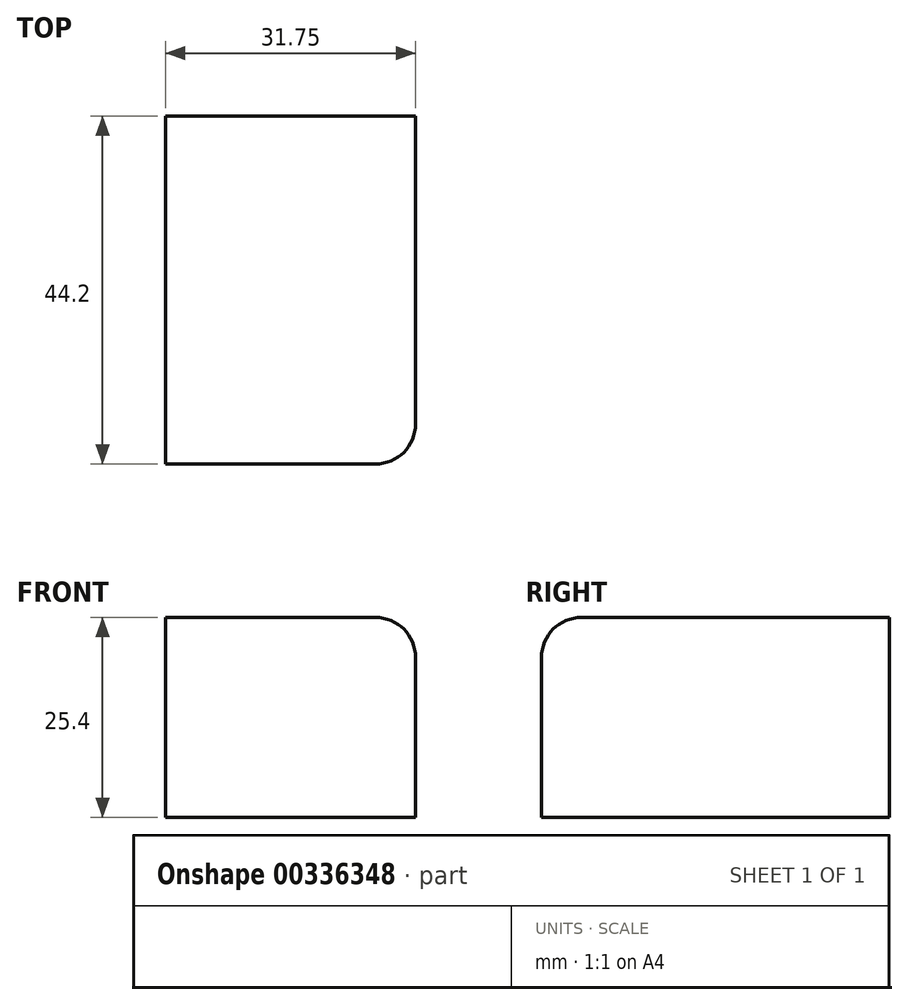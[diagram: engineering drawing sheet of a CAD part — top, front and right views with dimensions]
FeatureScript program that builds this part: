
annotation { "Feature Type Name" : "Feature", "Feature Type Description" : "" }
export const myFeature = defineFeature(function(context is Context, id is Id, definition is map)
    precondition{}
    {
        {
            var Q0;
            Q0=qCreatedBy(makeId("Front.planeOp"),FACE);
            var sketch = newSketch(context, id + "F0", { "sketchPlane" : qUnion([Q0])});
            skLineSegment(sketch, "E0.bottom", {"start": v(-12.7, 12.7) * mm, "end": v(19.05, 12.7) * mm});
            skLineSegment(sketch, "E0.top", {"start": v(-12.7, -12.7) * mm, "end": v(19.05, -12.7) * mm});
            skLineSegment(sketch, "E0.left", {"start": v(-12.7, 12.7) * mm, "end": v(-12.7, -12.7) * mm});
            skLineSegment(sketch, "E0.right", {"start": v(19.05, 12.7) * mm, "end": v(19.05, -12.7) * mm});
            skSolve(sketch);
        }
        {
            var Q0;
            Q0=makeQuery(id+"F0.imprint","IMPRINT",FACE,{"disambiguationData":[TD([[makeQuery(id+"F0.imprint","IMPRINT",EDGE,{"derivedFrom":sQuery(id+"F0.wireOp",EDGE,"E0.bottom")}),-1.0]])]});
            extrude(context, id + "F1", {"entities" : qUnion([Q0]), "depth" : 44.2 * mm});
        }
        {
            var Q0;
            Q0=makeQuery(id+"F1.opExtrude","CAP_EDGE",EDGE,{"disambiguationData":[OSD([sQuery(id+"F0.wireOp",EDGE,"E0.bottom")])],"isStart":false});
            var Q1;
            Q1=makeQuery(id+"F1.opExtrude","SWEPT_EDGE",EDGE,{"disambiguationData":[OSD([sQuery(id+"F0.wireOp",EDGE,"E0.bottom"),sQuery(id+"F0.wireOp",EDGE,"E0.right")])]});
            fillet(context, id + "F2", {"entities" : qUnion([Q0, Q1]), "radius" : 5.08 * mm, "tangentPropagation" : true, "allowEdgeOverflow" : false});
        }
        {
            var Q0;
            {var subQ0=sQuery(id+"F0.wireOp",EDGE,"E0.bottom");Q0=makeQuery(id+"F2.opFillet","BLEND_EDGE",EDGE,{"blendedFrom":[makeQuery(id+"F1.opExtrude","SWEPT_EDGE",EDGE,{"disambiguationData":[OSD([subQ0,sQuery(id+"F0.wireOp",EDGE,"E0.right")])]}),makeQuery(id+"F1.opExtrude","CAP_EDGE",EDGE,{"disambiguationData":[OSD([subQ0])],"isStart":false})],"blendedInto":[]});}
            fillet(context, id + "F3", {"entities" : qUnion([Q0]), "radius" : 5.08 * mm, "tangentPropagation" : true, "allowEdgeOverflow" : false});
        }
    });
